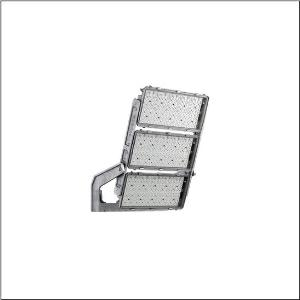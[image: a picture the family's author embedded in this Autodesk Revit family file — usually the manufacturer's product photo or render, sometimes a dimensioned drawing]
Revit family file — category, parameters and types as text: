
# Revit family: floodlight_fl_11_maxi_pro_remote___pl43_5xa779528a01aa_9860
name_source: partatom
category: Lighting Fixtures
units: mm (PartAtom-declared; Revit-internal decimal feet)

## family parameters
Cut with Voids When Loaded = No
Host = Face
Light Source = No
Part Type = Normal
Room Calculation Point = No
Round Connector Dimension = Use Diameter
Shared = No

## types (1)
- --- (1 x LED, 156040 lm, 1388 W, 5700K)
    Apparent Load = 1388 VA
    CIE Flux Codes = 25 74 99 100 100
    Color Rendering = 80
    Color Temperature = 5700K
    Default Elevation = 1800 mm
    Description = Floodlight FL 11  maxi  pro Remote floodlight; light control with lens of PMMA; cover panel of toughened safety glass, transparent; light distribution: PL43, asymmetric direct distribution, LEDcolour temperature: 5700K, rated luminous flux: 156.040lm, colour rendering: CRI > 80, light colour: 857; luminous efficacy: 112lm/W; brightness control: DMX+RDM; with terminal, 8-pole, max. 2.5mm², mains connection: 220..240V/380..400V AC, 50/60Hz, surge voltage resistance: line to ground: 10kV, ECG replaceable separately, LED unit replaceable without ESD environment, dustproof LED module, LED unit replaceable, LED unit replaceable on mast without ESD environment, dimming range 10..100%; 1388W floodlight with 3x LED unit of diecast aluminium, coated grey; length: 1.003mm / width: 651mm / height: 338mm; mounting bracket, of diecast aluminium, uncoated, natural, equipment: Power, protection rating (complete): IP66; insulation class (complete): insulation class I (protective earthing); certification: CE, ENEC, VDE; ball protection: ball impact resistance with accessories, impact resistance: IK07; only for outdoor installations, rated ambient temperature 10°C, permissible operating ambient temperature: -40..+30°C, permissible storage temperature: -40..+85°C; packaging unit: 1 piece

Light Distribution: PL43
    Height = 320 mm
    Lamp = 1 x LED
    Lamp Light Flux = 156040 lm
    Lamp Power = 1388 W
    Lamp count = 1
    Length = 1002 mm
    Luminous efficacy = 112 lm/W
    Manufacturer = Siteco
    ModVariant = No
    Model = 5XA779528A01AA
    Mounting Place = Ceiling
    Mounting Type = Surface mounted
    Number of Poles = 1
    OnlyDefault = Yes
    Power Factor = 1
    Product Name = Floodlight FL 11 maxi pro Remote | PL43
    Product group = floodlight | ceiling mounted
    ProductGroupID = 302
    Protection Class = Protection class I
    Protection Degree = IP 66
    RLX_Detail_Level = 1
    RLX_Emergency_Light_Flux = 0 lm
    RLX_Emergency_Type = 0
    RLX_Emergency_Type_DB = No
    RlxData = <blob elided: 52437 chars, md5=bd475111>
    Socket = socket
    Standby Power = 0 W
    System Light Flux = 156040 lm
    System Power = 1388 W
    Type Comments = factory setting: luminous flux: 100 % | dim-lin: 255 | 955 mA
    Type Image = l_1006784.jpg
    URL = http://relux.com
    VarID = @adj_050351
    Voltage = 0 V
    Weight = 0.00 kg
    Width = 655 mm

## geometry (parser evidence)
native form markers: Blend x4, Sweep x12
no freeform markers — native parametric forms only
